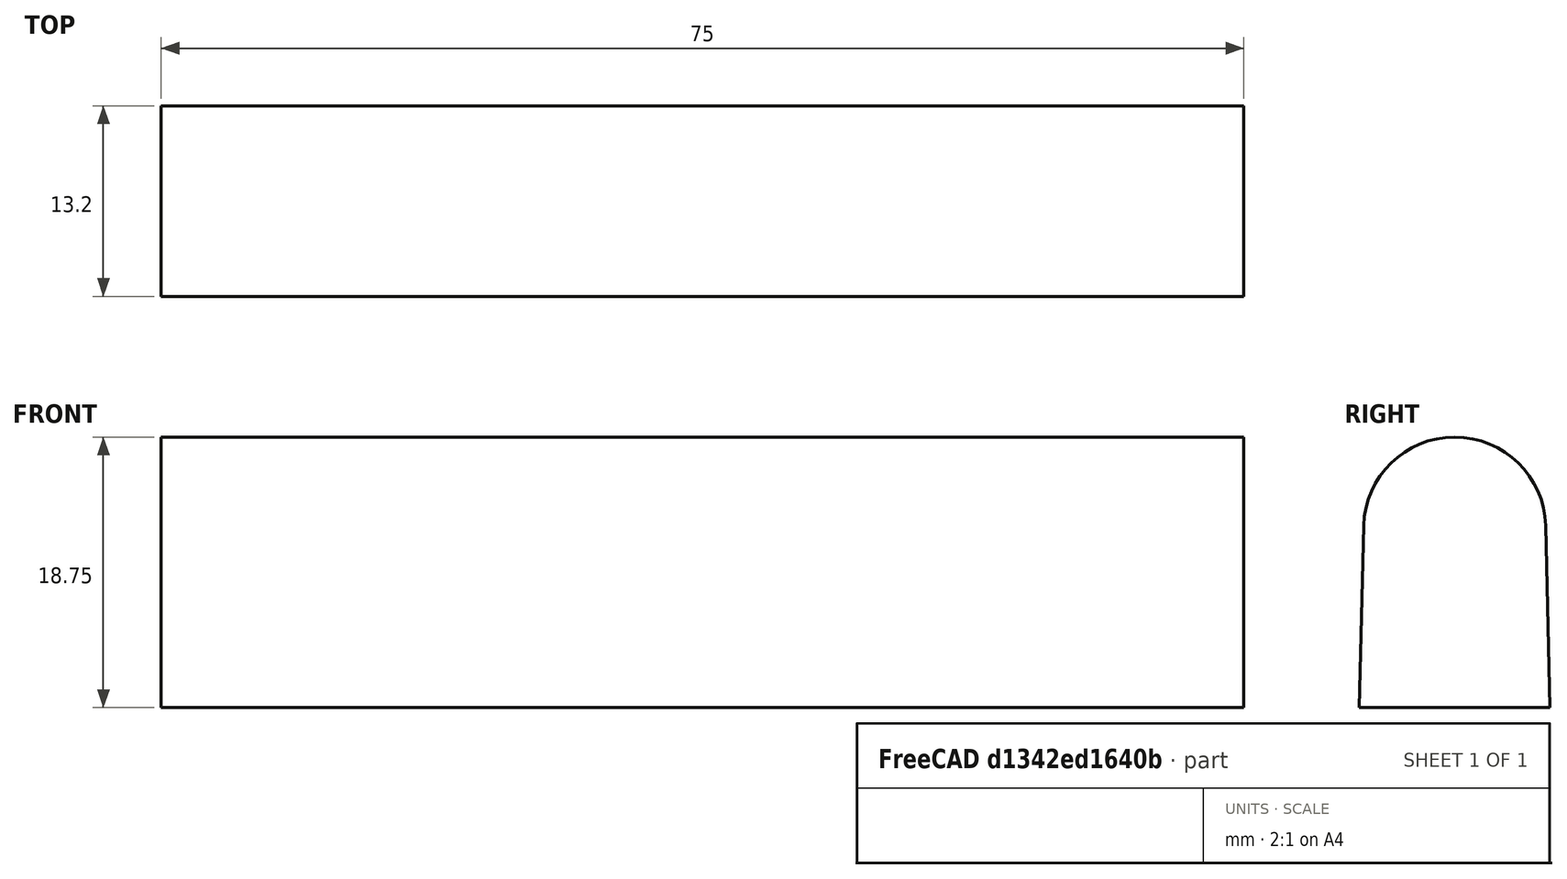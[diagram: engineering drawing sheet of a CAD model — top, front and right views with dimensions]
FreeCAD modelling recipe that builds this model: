
FCSTD DOCUMENT  (FreeCAD 0.21R33679 (Git))
Label: window_hinge_75mm
License: All rights reserved
LicenseURL: http://en.wikipedia.org/wiki/All_rights_reserved
objects: Sketcher::SketchObject×4, PartDesign::Body×2, PartDesign::SubShapeBinder×1, PartDesign::Pad×1, App::Part×1
note: 9 computed .brp shape members not serialized (recipe doc carries the construction recipe); baked Part::Feature solids carry a one-line shape summary decoded from their .brp

FEATURE [PartDesign::Body] Body
  Origin = -> Origin001
FEATURE [Sketcher::SketchObject] Sketch
  FullyConstrained = true
  sketch-geometry (2):
    g0: Circle CenterX=-30.5 CenterY=2 CenterZ=0 NormalX=0 NormalY=0 NormalZ=1 AngleXU=0 Radius=2.125
    g1: Circle CenterX=30.5 CenterY=2 CenterZ=0 NormalX=0 NormalY=0 NormalZ=1 AngleXU=0 Radius=2.125
  constraints (5):
    c: Symmetric(g0,g1,g-2)
    c: DistanceY(g1) = 2
    c: DistanceX(g0,g1) = 61
    c: Equal(g0,g1)
    c: Diameter(g0) = 4.25
FEATURE [Sketcher::SketchObject] Sketch001
  FullyConstrained = true
  sketch-geometry (3):
    g0: Circle CenterX=-18 CenterY=0 CenterZ=0 NormalX=0 NormalY=0 NormalZ=1 AngleXU=0 Radius=2.125
    g1: Circle CenterX=0 CenterY=0 CenterZ=0 NormalX=0 NormalY=0 NormalZ=1 AngleXU=0 Radius=2.125
    g2: Circle CenterX=18 CenterY=0 CenterZ=0 NormalX=0 NormalY=0 NormalZ=1 AngleXU=0 Radius=2.125
  constraints (7):
    c: Coincident(g1,g-1)
    c: PointOnObject(g2,g-1)
    c: Equal(g0,g1)
    c: Equal(g0,g2)
    c: Diameter(g0) = 4.25
    c: Symmetric(g0,g2,g-2)
    c: DistanceX(g0,g2) = 36
FEATURE [PartDesign::SubShapeBinder] Binder
  BindCopyOnChange = 0
  BindMode = 0
  ClaimChildren = false
  Context = -> Part [Body001.Binder.]
  Fuse = false
  MakeFace = true
  OffsetFill = false
  OffsetIntersection = false
  OffsetJoinType = 0
  OffsetOpenResult = false
  PartialLoad = false
  Relative = true
  Support = -> [Sketch001]
  _Version = 2
FEATURE [Sketcher::SketchObject] Sketch002
  FullyConstrained = true
  MapMode = 5
  Placement = pos=(0,0,0) rot=(0.57735,0.57735,0.57735;2.0944rad)
  Support = -> [YZ_Plane002]
  sketch-geometry (5):
    g0: ArcOfCircle CenterX=0 CenterY=12.45 CenterZ=0 NormalX=0 NormalY=0 NormalZ=1 AngleXU=0 Radius=6.3 StartAngle=0.0239467 EndAngle=3.11765
    g1: LineSegment StartX=-6.29819 StartY=12.6008 StartZ=0 EndX=-6.6 EndY=0 EndZ=0
    g2: LineSegment StartX=-6.6 StartY=0 StartZ=0 EndX=6.6 EndY=0 EndZ=0
    g3: LineSegment StartX=6.6 StartY=0 StartZ=0 EndX=6.29819 EndY=12.6008 EndZ=0
    g4: GeomPoint X=0 Y=18.75 Z=0
  constraints (12):
    c: PointOnObject(g0,g-2)
    c: Tangent(g0,g1) = -1.5708
    c: Coincident(g1,g2)
    c: PointOnObject(g2,g-1)
    c: Coincident(g2,g3)
    c: Tangent(g3,g0) = -1.5708
    c: DistanceX(g2,g2) = 13.2
    c: Symmetric(g1,g2,g-2)
    c: Diameter(g0) = 12.6
    c: PointOnObject(g4,g-2)
    c: PointOnObject(g4,g0)
    c: DistanceY(g4) = 18.75
FEATURE [PartDesign::Pad] Pad
  Direction = (1,-2e-16,3e-16)
  Length = 75
  Length2 = 10
  Midplane = true
  Placement = pos=(0,0,0) rot=(0.57735,0.57735,0.57735;2.0944rad)
  Profile = -> Sketch002
  ReferenceAxis = -> Sketch002 [N_Axis]
  Type = 0
FEATURE [Sketcher::SketchObject] Sketch003
  FullyConstrained = true
  MapMode = 5
  Placement = pos=(0,0,0) rot=(0.57735,0.57735,0.57735;2.0944rad)
  Support = -> [YZ_Plane002]
FEATURE [PartDesign::Body] Body001
  Group = -> [Binder,Sketch002,Pad,Sketch003]
  Origin = -> Origin002
  Tip = -> Pad
FEATURE [App::Part] Part
  Group = -> [Body,Body001]
  Origin = -> Origin
